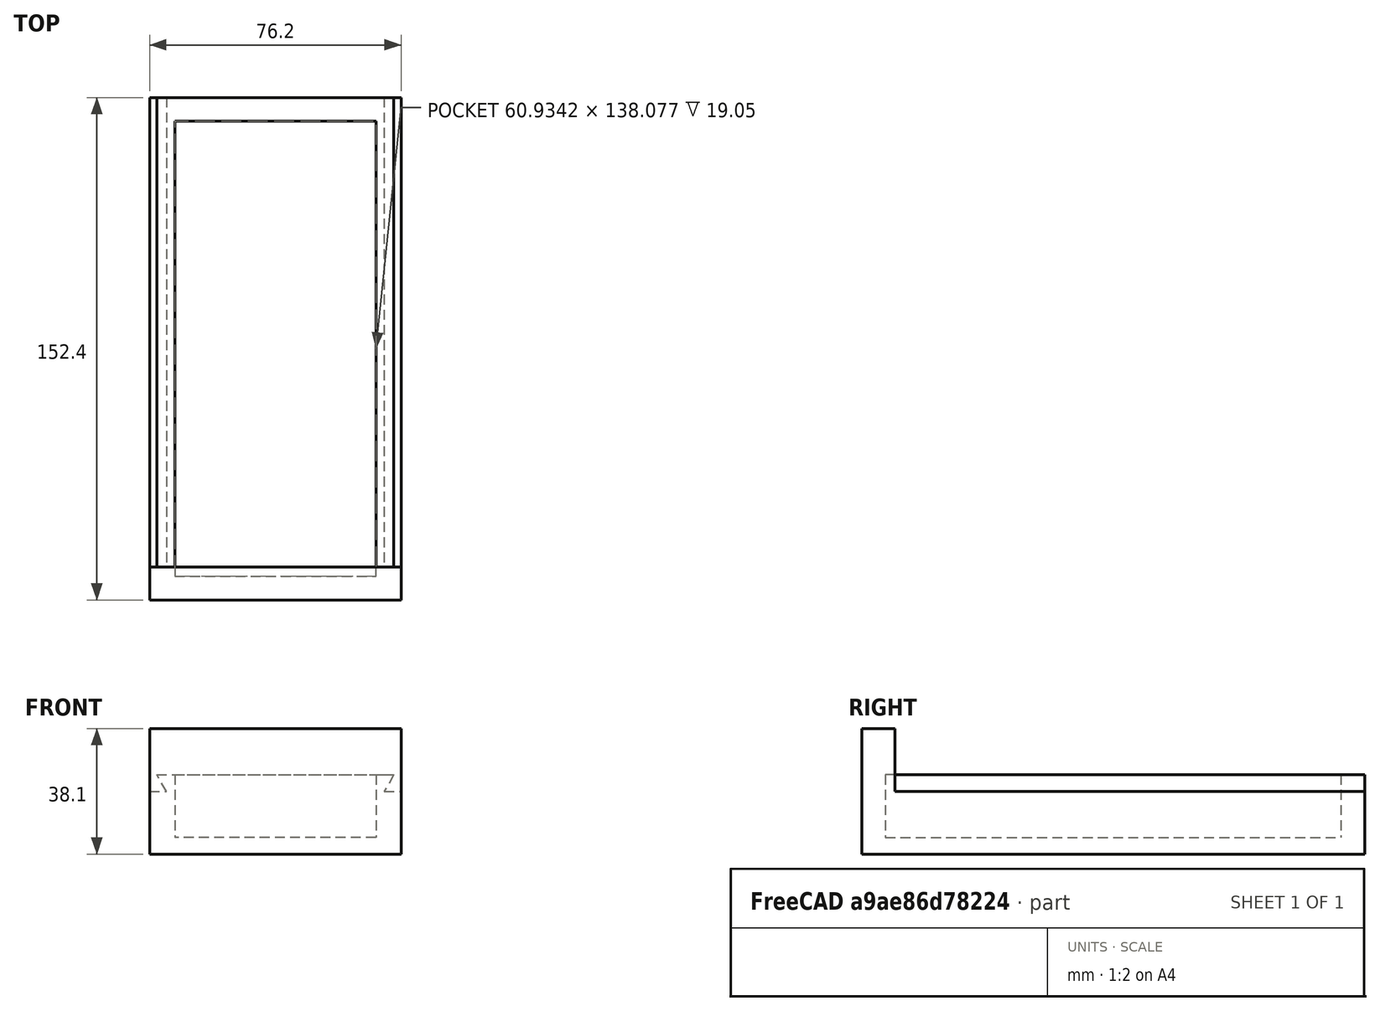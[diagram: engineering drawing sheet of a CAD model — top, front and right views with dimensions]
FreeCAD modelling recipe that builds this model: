
FCSTD DOCUMENT  (FreeCAD 0.21R33771 (Git))
Label: 9mmAmmo
License: All rights reserved
LicenseURL: http://en.wikipedia.org/wiki/All_rights_reserved
objects: TechDraw::DrawViewDimension×19, Sketcher::SketchObject×5, TechDraw::DrawViewPart×4, PartDesign::Pocket×3, PartDesign::Body×2, App::Part×2, PartDesign::Pad×1, TechDraw::DrawSVGTemplate×1, TechDraw::DrawPage×1
note: 42 computed .brp shape members not serialized (recipe doc carries the construction recipe); baked Part::Feature solids carry a one-line shape summary decoded from their .brp

FEATURE [Sketcher::SketchObject] Sketch  label="Box Sketch"
  FullyConstrained = true
  MapMode = 5
  Support = -> [XY_Plane001]
  sketch-geometry (5):
    g0: LineSegment StartX=-38.1 StartY=76.2 StartZ=0 EndX=-38.1 EndY=-76.2 EndZ=0
    g1: LineSegment StartX=-38.1 StartY=-76.2 StartZ=0 EndX=38.1 EndY=-76.2 EndZ=0
    g2: LineSegment StartX=38.1 StartY=-76.2 StartZ=0 EndX=38.1 EndY=76.2 EndZ=0
    g3: LineSegment StartX=38.1 StartY=76.2 StartZ=0 EndX=-38.1 EndY=76.2 EndZ=0
    g4: GeomPoint X=0 Y=0 Z=0
  constraints (12):
    c: Coincident(g0,g1)
    c: Coincident(g1,g2)
    c: Coincident(g2,g3)
    c: Coincident(g3,g0)
    c: Horizontal(g1)
    c: Horizontal(g3)
    c: Vertical(g0)
    c: Vertical(g2)
    c: Symmetric(g1,g0,g4)
    c: Coincident(g4,g-1)
    c: DistanceY(g0,g0) = 152.4
    c: DistanceX(g3,g3) = 76.2
FEATURE [PartDesign::Pad] Pad  label="Box Pad"
  Direction = (0,0,1)
  Length = 38.1
  Length2 = 10
  Profile = -> Sketch
  ReferenceAxis = -> Sketch [N_Axis]
  Type = 0
FEATURE [Sketcher::SketchObject] Sketch001  label="Length Cutaway Sketch"
  AttachmentOffset = pos=(0,0,-76.2) rot=(0,0,1;0rad)
  FullyConstrained = false
  MapMode = 5
  Placement = pos=(0,76.2,1.69e-14) rot=(1,0,0;1.5708rad)
  Support = -> [XZ_Plane001]
  expr: .AttachmentOffset.Base.z = -152.4 / 2
  expr: Constraints[10] = 38.1 / 2 + 5
  sketch-geometry (5):
    g0: LineSegment StartX=-45.6181 StartY=45.1482 StartZ=0 EndX=-45.6181 EndY=24.05 EndZ=0
    g1: LineSegment StartX=-45.6181 StartY=24.05 StartZ=0 EndX=45.6181 EndY=24.05 EndZ=0
    g2: LineSegment StartX=45.6181 StartY=24.05 StartZ=0 EndX=45.6181 EndY=45.1482 EndZ=0
    g3: LineSegment StartX=45.6181 StartY=45.1482 StartZ=0 EndX=-45.6181 EndY=45.1482 EndZ=0
    g4: GeomPoint X=0 Y=34.5991 Z=0
  constraints (11):
    c: Coincident(g0,g1)
    c: Coincident(g1,g2)
    c: Coincident(g2,g3)
    c: Coincident(g3,g0)
    c: Horizontal(g1)
    c: Horizontal(g3)
    c: Vertical(g0)
    c: Vertical(g2)
    c: Symmetric(g1,g0,g4)
    c: PointOnObject(g4,g-2)
    c: DistanceY(g-1,g1) = 24.05
FEATURE [PartDesign::Pocket] Pocket  label="Length Cutaway Pocket"
  BaseFeature = -> Pad
  Direction = (0,1,-2e-16)
  Length = 142.4
  Length2 = 5
  Profile = -> Sketch001
  ReferenceAxis = -> Sketch001 [N_Axis]
  Reversed = true
  Type = 0
  expr: Length = 152.4 - 10
FEATURE [Sketcher::SketchObject] Sketch002  label="Dovetail Ammoside Sketch"
  AttachmentOffset = pos=(0,0,-76.2) rot=(0,0,1;0rad)
  FullyConstrained = true
  MapMode = 5
  Placement = pos=(0,76.2,1.69e-14) rot=(1,0,0;1.5708rad)
  Support = -> [XZ_Plane001]
  sketch-geometry (8):
    g0: LineSegment StartX=-33 StartY=19 StartZ=0 EndX=-35.9445 EndY=24.1 EndZ=0
    g1: LineSegment StartX=-38.2 StartY=19 StartZ=0 EndX=-33 EndY=19 EndZ=0
    g2: LineSegment StartX=33 StartY=19 StartZ=0 EndX=38.2 EndY=19 EndZ=0
    g3: LineSegment StartX=38.2 StartY=24.1 StartZ=0 EndX=35.9445 EndY=24.1 EndZ=0
    g4: LineSegment StartX=38.2 StartY=24.1 StartZ=0 EndX=38.2 EndY=19 EndZ=0
    g5: LineSegment StartX=35.9445 StartY=24.1 StartZ=0 EndX=33 EndY=19 EndZ=0
    g6: LineSegment StartX=-35.9445 StartY=24.1 StartZ=0 EndX=-38.2 EndY=24.1 EndZ=0
    g7: LineSegment StartX=-38.2 StartY=24.1 StartZ=0 EndX=-38.2 EndY=19 EndZ=0
  constraints (24):
    c: Coincident(g1,g0)
    c: Horizontal(g1)
    c: DistanceX(g0,g-1) = 33
    c: Coincident(g5,g2)
    c: Horizontal(g2)
    c: Horizontal(g2,g0)
    c: DistanceX(g-1,g2) = 33
    c: Coincident(g4,g3)
    c: Coincident(g5,g3)
    c: Coincident(g2,g4)
    c: Angle(g2,g5) = 1.0472
    c: Coincident(g7,g6)
    c: Horizontal(g6)
    c: Coincident(g0,g6)
    c: Coincident(g1,g7)
    c: Angle(g0,g1) = 1.0472
    c: DistanceY(g-1,g0) = 24.1
    c: DistanceX(g1,g1) = 5.2
    c: DistanceY(g-1,g0) = 19
    c: Vertical(g7)
    c: Vertical(g4)
    c: DistanceY(g-1,g3) = 24.1
    c: Horizontal(g3)
    c: DistanceX(g2,g2) = 5.2
FEATURE [PartDesign::Pocket] Pocket001  label="Dovetail Ammoside Pocket"
  BaseFeature = -> Pocket
  Direction = (0,1,-2e-16)
  Length = 142.4
  Length2 = 5
  Profile = -> Sketch002
  ReferenceAxis = -> Sketch002 [N_Axis]
  Reversed = true
  Type = 0
  expr: Length = 152.4 - 10
FEATURE [Sketcher::SketchObject] Sketch003  label="Ammo Storage Sketch"
  AttachmentOffset = pos=(0,0,24.05) rot=(0,0,1;0rad)
  FullyConstrained = false
  MapMode = 5
  Placement = pos=(0,0,24.05) rot=(0,0,1;0rad)
  Support = -> [XY_Plane001]
  expr: .AttachmentOffset.Base.z = 38.1 / 2 + 5
  sketch-geometry (5):
    g0: LineSegment StartX=-30.4671 StartY=69.0383 StartZ=0 EndX=-30.4671 EndY=-69.0383 EndZ=0
    g1: LineSegment StartX=-30.4671 StartY=-69.0383 StartZ=0 EndX=30.4671 EndY=-69.0383 EndZ=0
    g2: LineSegment StartX=30.4671 StartY=-69.0383 StartZ=0 EndX=30.4671 EndY=69.0383 EndZ=0
    g3: LineSegment StartX=30.4671 StartY=69.0383 StartZ=0 EndX=-30.4671 EndY=69.0383 EndZ=0
    g4: GeomPoint X=0 Y=0 Z=0
  constraints (10):
    c: Coincident(g0,g1)
    c: Coincident(g1,g2)
    c: Coincident(g2,g3)
    c: Coincident(g3,g0)
    c: Horizontal(g1)
    c: Horizontal(g3)
    c: Vertical(g0)
    c: Vertical(g2)
    c: Symmetric(g1,g0,g4)
    c: Coincident(g4,g-1)
FEATURE [PartDesign::Pocket] Pocket002  label="Ammo Storage Pocket"
  BaseFeature = -> Pocket001
  Direction = (0,0,-1)
  Length = 19.05
  Length2 = 5
  Profile = -> Sketch003
  ReferenceAxis = -> Sketch003 [N_Axis]
  Type = 0
  expr: Length = 38.1 / 2
FEATURE [PartDesign::Body] Body  label="9mmAmmoBox Body"
  Group = -> [Sketch,Pad,Sketch001,Pocket,Sketch002,Pocket001,Sketch003,Pocket002]
  Origin = -> Origin001
  Tip = -> Pocket002
FEATURE [App::Part] Part  label="9mmAmmoBox"
  Group = -> [Body]
  Origin = -> Origin
FEATURE [TechDraw::DrawSVGTemplate] Template
  EditableTexts = CompanyName=Michael H Roberts; DrawingTitle1=9mm Ammo Box; DrawnBy=MR; Scale=Scale
  Height = 215.9
  Orientation = 1
  Template = <path>
  Width = 279.4
FEATURE [TechDraw::DrawViewPart] View  label="Iso View"
  Caption = Iso View
  CoarseView = false
  Direction = (0.57735,-0.57735,0.57735)
  Focus = 100
  HardHidden = false
  IsoCount = 0
  IsoHidden = false
  IsoVisible = false
  LockPosition = false
  Perspective = false
  Rotation = 0
  Scale = 0.6
  ScaleType = 2
  ScrubCount = 0
  SeamHidden = false
  SeamVisible = true
  SmoothHidden = false
  SmoothVisible = true
  Source = -> [Pocket002]
  X = 199.933
  XDirection = (0.707107,0.707107,0)
  Y = 158.963
FEATURE [TechDraw::DrawViewPart] View001  label="Top View"
  Caption = Top View
  CoarseView = false
  Direction = (0,0,1)
  Focus = 100
  HardHidden = false
  IsoCount = 0
  IsoHidden = false
  IsoVisible = false
  LockPosition = false
  Perspective = false
  Rotation = 90
  Scale = 0.7
  ScaleType = 2
  ScrubCount = 0
  SeamHidden = false
  SeamVisible = true
  SmoothHidden = false
  SmoothVisible = true
  Source = -> [Pocket002]
  X = 87.6152
  XDirection = (1,0,0)
  Y = 156.643
FEATURE [TechDraw::DrawViewPart] View002  label="Side View"
  Caption = Side View
  CoarseView = false
  Direction = (1,0,0)
  Focus = 100
  HardHidden = false
  IsoCount = 0
  IsoHidden = false
  IsoVisible = false
  LockPosition = false
  Perspective = false
  Rotation = 0
  Scale = 0.7
  ScaleType = 2
  ScrubCount = 0
  SeamHidden = false
  SeamVisible = true
  SmoothHidden = false
  SmoothVisible = true
  Source = -> [Pocket002]
  X = 193.586
  XDirection = (0,1,0)
  Y = 97.1228
FEATURE [TechDraw::DrawViewPart] View003  label="Back View"
  Caption = Back View
  CoarseView = false
  Direction = (0,1,0)
  Focus = 100
  HardHidden = false
  IsoCount = 0
  IsoHidden = false
  IsoVisible = false
  LockPosition = false
  Perspective = false
  Rotation = 0
  ScaleType = 2
  ScrubCount = 0
  SeamHidden = false
  SeamVisible = true
  SmoothHidden = false
  SmoothVisible = true
  Source = -> [Pocket002]
  X = 80.7252
  XDirection = (-1,0,0)
  Y = 87.9552
FEATURE [TechDraw::DrawViewDimension] Dimension001
  AngleOverride = false
  Arbitrary = false
  ArbitraryTolerances = false
  EqualTolerance = true
  ExtensionAngle = 0
  FormatSpec = %.3f
  FormatSpecOverTolerance = %+.3f
  FormatSpecUnderTolerance = %+.3f
  Inverted = false
  LineAngle = 0
  LockPosition = false
  MeasureType = 1
  OverTolerance = 0
  References2D = -> [View001]
  Rotation = 0
  ScaleType = 2
  TheoreticalExact = false
  Type = 1
  UnderTolerance = 0
  X = -0.913011
  Y = 33.7511
FEATURE [TechDraw::DrawViewDimension] Dimension002
  AngleOverride = false
  Arbitrary = false
  ArbitraryTolerances = false
  EqualTolerance = true
  ExtensionAngle = 0
  FormatSpec = %.3f
  FormatSpecOverTolerance = %+.3f
  FormatSpecUnderTolerance = %+.3f
  Inverted = false
  LineAngle = 0
  LockPosition = false
  MeasureType = 1
  OverTolerance = 0
  References2D = -> [View001]
  Rotation = 0
  ScaleType = 2
  TheoreticalExact = false
  Type = 1
  UnderTolerance = 0
  X = 34.5526
  Y = 35.6124
FEATURE [TechDraw::DrawViewDimension] Dimension
  AngleOverride = false
  Arbitrary = false
  ArbitraryTolerances = false
  EqualTolerance = true
  ExtensionAngle = 0
  FormatSpec = %.3f
  FormatSpecOverTolerance = %+.3f
  FormatSpecUnderTolerance = %+.3f
  Inverted = false
  LineAngle = 0
  LockPosition = false
  MeasureType = 1
  OverTolerance = 0
  References2D = -> [View001]
  Rotation = 0
  ScaleType = 2
  TheoreticalExact = false
  Type = 2
  UnderTolerance = 0
  X = -44.0518
  Y = 10.6792
FEATURE [TechDraw::DrawViewDimension] Dimension003
  AngleOverride = false
  Arbitrary = false
  ArbitraryTolerances = false
  EqualTolerance = true
  ExtensionAngle = 0
  FormatSpec = %.3f
  FormatSpecOverTolerance = %+.3f
  FormatSpecUnderTolerance = %+.3f
  Inverted = false
  LineAngle = 0
  LockPosition = false
  MeasureType = 1
  OverTolerance = 0
  References2D = -> [View001]
  Rotation = 0
  ScaleType = 2
  TheoreticalExact = false
  Type = 2
  UnderTolerance = 0
  X = -36.2857
  Y = 10.426
FEATURE [TechDraw::DrawViewDimension] Dimension004
  AngleOverride = false
  Arbitrary = false
  ArbitraryTolerances = false
  EqualTolerance = true
  ExtensionAngle = 0
  FormatSpec = %.3f
  FormatSpecOverTolerance = %+.3f
  FormatSpecUnderTolerance = %+.3f
  Inverted = false
  LineAngle = 0
  LockPosition = false
  MeasureType = 1
  OverTolerance = 0
  References2D = -> [View001]
  Rotation = 0
  ScaleType = 2
  TheoreticalExact = false
  Type = 2
  UnderTolerance = 0
  X = -36.4907
  Y = -9.68571
FEATURE [TechDraw::DrawViewDimension] Dimension005
  AngleOverride = false
  Arbitrary = false
  ArbitraryTolerances = false
  EqualTolerance = true
  ExtensionAngle = 0
  FormatSpec = %.3f
  FormatSpecOverTolerance = %+.3f
  FormatSpecUnderTolerance = %+.3f
  Inverted = false
  LineAngle = 0
  LockPosition = false
  MeasureType = 1
  OverTolerance = 0
  References2D = -> [View001]
  Rotation = 0
  ScaleType = 2
  TheoreticalExact = false
  Type = 1
  UnderTolerance = 0
  X = -33.7236
  Y = 37.1378
FEATURE [TechDraw::DrawViewDimension] Dimension006
  AngleOverride = false
  Arbitrary = false
  ArbitraryTolerances = false
  EqualTolerance = true
  ExtensionAngle = 0
  FormatSpec = %.3f
  FormatSpecOverTolerance = %+.3f
  FormatSpecUnderTolerance = %+.3f
  Inverted = false
  LineAngle = 0
  LockPosition = false
  MeasureType = 1
  OverTolerance = 0
  References2D = -> [View001]
  Rotation = 0
  ScaleType = 2
  TheoreticalExact = false
  Type = 2
  UnderTolerance = 0
  X = 39.136
  Y = 10.0505
FEATURE [TechDraw::DrawViewDimension] Dimension007
  AngleOverride = false
  Arbitrary = false
  ArbitraryTolerances = false
  EqualTolerance = true
  ExtensionAngle = 0
  FormatSpec = %.3f
  FormatSpecOverTolerance = %+.3f
  FormatSpecUnderTolerance = %+.3f
  Inverted = false
  LineAngle = 0
  LockPosition = false
  MeasureType = 1
  OverTolerance = 0
  References2D = -> [View001]
  Rotation = 0
  ScaleType = 2
  TheoreticalExact = false
  Type = 2
  UnderTolerance = 0
  X = -16.1272
  Y = 10.2177
FEATURE [TechDraw::DrawViewDimension] Dimension008
  AngleOverride = false
  Arbitrary = false
  ArbitraryTolerances = false
  EqualTolerance = true
  ExtensionAngle = 0
  FormatSpec = %.3f
  FormatSpecOverTolerance = %+.3f
  FormatSpecUnderTolerance = %+.3f
  Inverted = false
  LineAngle = 0
  LockPosition = false
  MeasureType = 1
  OverTolerance = 0
  References2D = -> [View001]
  Rotation = 0
  ScaleType = 2
  TheoreticalExact = false
  Type = 1
  UnderTolerance = 0
  X = 6.88151
  Y = 0.598297
FEATURE [TechDraw::DrawViewDimension] Dimension009
  AngleOverride = false
  Arbitrary = false
  ArbitraryTolerances = false
  EqualTolerance = true
  ExtensionAngle = 0
  FormatSpec = %.3f
  FormatSpecOverTolerance = %+.3f
  FormatSpecUnderTolerance = %+.3f
  Inverted = false
  LineAngle = 0
  LockPosition = false
  MeasureType = 1
  OverTolerance = 0
  References2D = -> [View003]
  Rotation = 0
  ScaleType = 2
  TheoreticalExact = false
  Type = 1
  UnderTolerance = 0
  X = -22.9898
  Y = -10.6059
FEATURE [TechDraw::DrawViewDimension] Dimension010
  AngleOverride = false
  Arbitrary = false
  ArbitraryTolerances = false
  EqualTolerance = true
  ExtensionAngle = 0
  FormatSpec = %.3f
  FormatSpecOverTolerance = %+.3f
  FormatSpecUnderTolerance = %+.3f
  Inverted = false
  LineAngle = 0
  LockPosition = false
  MeasureType = 1
  OverTolerance = 0
  References2D = -> [View003]
  Rotation = 0
  ScaleType = 2
  TheoreticalExact = false
  Type = 1
  UnderTolerance = 0
  X = 0.189865
  Y = -4.63277
FEATURE [TechDraw::DrawViewDimension] Dimension011
  AngleOverride = false
  Arbitrary = false
  ArbitraryTolerances = false
  EqualTolerance = true
  ExtensionAngle = 0
  FormatSpec = %.3f
  FormatSpecOverTolerance = %+.3f
  FormatSpecUnderTolerance = %+.3f
  Inverted = false
  LineAngle = 0
  LockPosition = false
  MeasureType = 1
  OverTolerance = 0
  References2D = -> [View003]
  Rotation = 0
  ScaleType = 2
  TheoreticalExact = false
  Type = 1
  UnderTolerance = 0
  X = -0.695589
  Y = 1.00606
FEATURE [TechDraw::DrawViewDimension] Dimension012
  AngleOverride = false
  Arbitrary = false
  ArbitraryTolerances = false
  EqualTolerance = true
  ExtensionAngle = 0
  FormatSpec = %.3f
  FormatSpecOverTolerance = %+.3f
  FormatSpecUnderTolerance = %+.3f
  Inverted = false
  LineAngle = 0
  LockPosition = false
  MeasureType = 1
  OverTolerance = 0
  References2D = -> [View003]
  Rotation = 0
  ScaleType = 2
  TheoreticalExact = false
  Type = 6
  UnderTolerance = 0
  X = 47.3901
  Y = 8.83623
FEATURE [TechDraw::DrawViewDimension] Dimension013
  AngleOverride = false
  Arbitrary = false
  ArbitraryTolerances = false
  EqualTolerance = true
  ExtensionAngle = 0
  FormatSpec = %.3f
  FormatSpecOverTolerance = %+.3f
  FormatSpecUnderTolerance = %+.3f
  Inverted = false
  LineAngle = 0
  LockPosition = false
  MeasureType = 1
  OverTolerance = 0
  References2D = -> [View002]
  Rotation = 0
  ScaleType = 2
  TheoreticalExact = false
  Type = 2
  UnderTolerance = 0
  X = -44.2321
  Y = 1
FEATURE [TechDraw::DrawViewDimension] Dimension014
  AngleOverride = false
  Arbitrary = false
  ArbitraryTolerances = false
  EqualTolerance = true
  ExtensionAngle = 0
  FormatSpec = %.3f
  FormatSpecOverTolerance = %+.3f
  FormatSpecUnderTolerance = %+.3f
  Inverted = false
  LineAngle = 0
  LockPosition = false
  MeasureType = 1
  OverTolerance = 0
  References2D = -> [View002]
  Rotation = 0
  ScaleType = 2
  TheoreticalExact = false
  Type = 1
  UnderTolerance = 0
  X = 0.766509
  Y = -3.41494
FEATURE [TechDraw::DrawViewDimension] Dimension015
  AngleOverride = false
  Arbitrary = false
  ArbitraryTolerances = false
  EqualTolerance = true
  ExtensionAngle = 0
  FormatSpec = %.3f
  FormatSpecOverTolerance = %+.3f
  FormatSpecUnderTolerance = %+.3f
  Inverted = false
  LineAngle = 0
  LockPosition = false
  MeasureType = 1
  OverTolerance = 0
  References2D = -> [View003]
  Rotation = 0
  ScaleType = 2
  TheoreticalExact = false
  Type = 2
  UnderTolerance = 0
  X = -47.4831
  Y = 21.2989
FEATURE [TechDraw::DrawViewDimension] Dimension016
  AngleOverride = false
  Arbitrary = false
  ArbitraryTolerances = false
  EqualTolerance = true
  ExtensionAngle = 0
  FormatSpec = %.3f
  FormatSpecOverTolerance = %+.3f
  FormatSpecUnderTolerance = %+.3f
  Inverted = false
  LineAngle = 0
  LockPosition = false
  MeasureType = 1
  OverTolerance = 0
  References2D = -> [View003]
  Rotation = 0
  ScaleType = 2
  TheoreticalExact = false
  Type = 1
  UnderTolerance = 0
  X = -8.98663
  Y = 16.9215
FEATURE [TechDraw::DrawViewDimension] Dimension017
  AngleOverride = false
  Arbitrary = false
  ArbitraryTolerances = false
  EqualTolerance = true
  ExtensionAngle = 0
  FormatSpec = %.3f
  FormatSpecOverTolerance = %+.3f
  FormatSpecUnderTolerance = %+.3f
  Inverted = false
  LineAngle = 0
  LockPosition = false
  MeasureType = 1
  OverTolerance = 0
  References2D = -> [View003]
  Rotation = 0
  ScaleType = 2
  TheoreticalExact = false
  Type = 1
  UnderTolerance = 0
  X = -0.526966
  Y = 9.49182
FEATURE [TechDraw::DrawViewDimension] Dimension018
  AngleOverride = false
  Arbitrary = false
  ArbitraryTolerances = false
  EqualTolerance = true
  ExtensionAngle = 0
  FormatSpec = %.3f
  FormatSpecOverTolerance = %+.3f
  FormatSpecUnderTolerance = %+.3f
  Inverted = false
  LineAngle = 0
  LockPosition = false
  MeasureType = 1
  OverTolerance = 0
  References2D = -> [View003]
  Rotation = 0
  ScaleType = 2
  TheoreticalExact = false
  Type = 1
  UnderTolerance = 0
  X = 7.0712
  Y = 14.3874
FEATURE [TechDraw::DrawPage] Page
  KeepUpdated = true
  NextBalloonIndex = 1
  ProjectionType = 0
  Template = -> Template
  Views = -> [View,View001,View002,View003,Dimension001,Dimension002,Dimension,Dimension003,Dimension004,Dimension005,Dimension006,Dimension007,Dimension008,Dimension009,Dimension010,Dimension011,Dimension012,Dimension013,Dimension014,Dimension015,Dimension016,Dimension017,Dimension018]
FEATURE [Sketcher::SketchObject] Sketch004
  AttachmentOffset = pos=(0,0,-76.2) rot=(0,0,1;0rad)
  FullyConstrained = false
  MapMode = 5
  Placement = pos=(0,76.2,-1.69e-14) rot=(1,0,0;1.5708rad)
  Support = -> [XZ_Plane003]
  sketch-geometry (9):
    g0: LineSegment StartX=-34.1988 StartY=19.6171 StartZ=0 EndX=-37.9065 EndY=19.6171 EndZ=0
    g1: LineSegment StartX=-37.9065 StartY=19.6171 StartZ=0 EndX=-37.9065 EndY=27.0325 EndZ=0
    g2: LineSegment StartX=-37.9065 StartY=27.0325 StartZ=0 EndX=38.0992 EndY=27.0325 EndZ=0
    g3: LineSegment StartX=38.0992 StartY=27.0325 StartZ=0 EndX=38.0992 EndY=19.0674 EndZ=0
    g4: LineSegment StartX=38.0992 StartY=19.0674 StartZ=0 EndX=33.2014 EndY=19.0674 EndZ=0
    g5: LineSegment StartX=33.2014 StartY=19.0674 StartZ=0 EndX=36.1829 EndY=24.2315 EndZ=0
    g6: LineSegment StartX=36.1829 StartY=24.2315 StartZ=0 EndX=-34.8572 EndY=24.2315 EndZ=0
    g7: LineSegment StartX=-34.8572 StartY=24.2315 StartZ=0 EndX=-35.9909 EndY=23.3866 EndZ=0
    g8: LineSegment StartX=-35.9909 StartY=23.3866 StartZ=0 EndX=-34.1988 EndY=19.6171 EndZ=0
  constraints (16):
    c: Horizontal(g0)
    c: Coincident(g1,g0)
    c: Vertical(g1)
    c: Coincident(g2,g1)
    c: Horizontal(g2)
    c: Coincident(g3,g2)
    c: Vertical(g3)
    c: Coincident(g4,g3)
    c: Horizontal(g4)
    c: Coincident(g5,g4)
    c: Horizontal(g6)
    c: Coincident(g7,g6)
    c: Coincident(g8,g7)
    c: Coincident(g8,g0)
    c: Coincident(g6,g5)
    c: Angle(g4,g5) = 1.0472
FEATURE [PartDesign::Body] Body001  label="Body"
  Group = -> [Sketch004]
  Origin = -> Origin003
FEATURE [App::Part] Part001  label="9mmAmmoBoxTop"
  Group = -> [Body001]
  Origin = -> Origin002
note: 1 file-system path scrubbed to <path> (originals preserved in the JSON sidecar)
